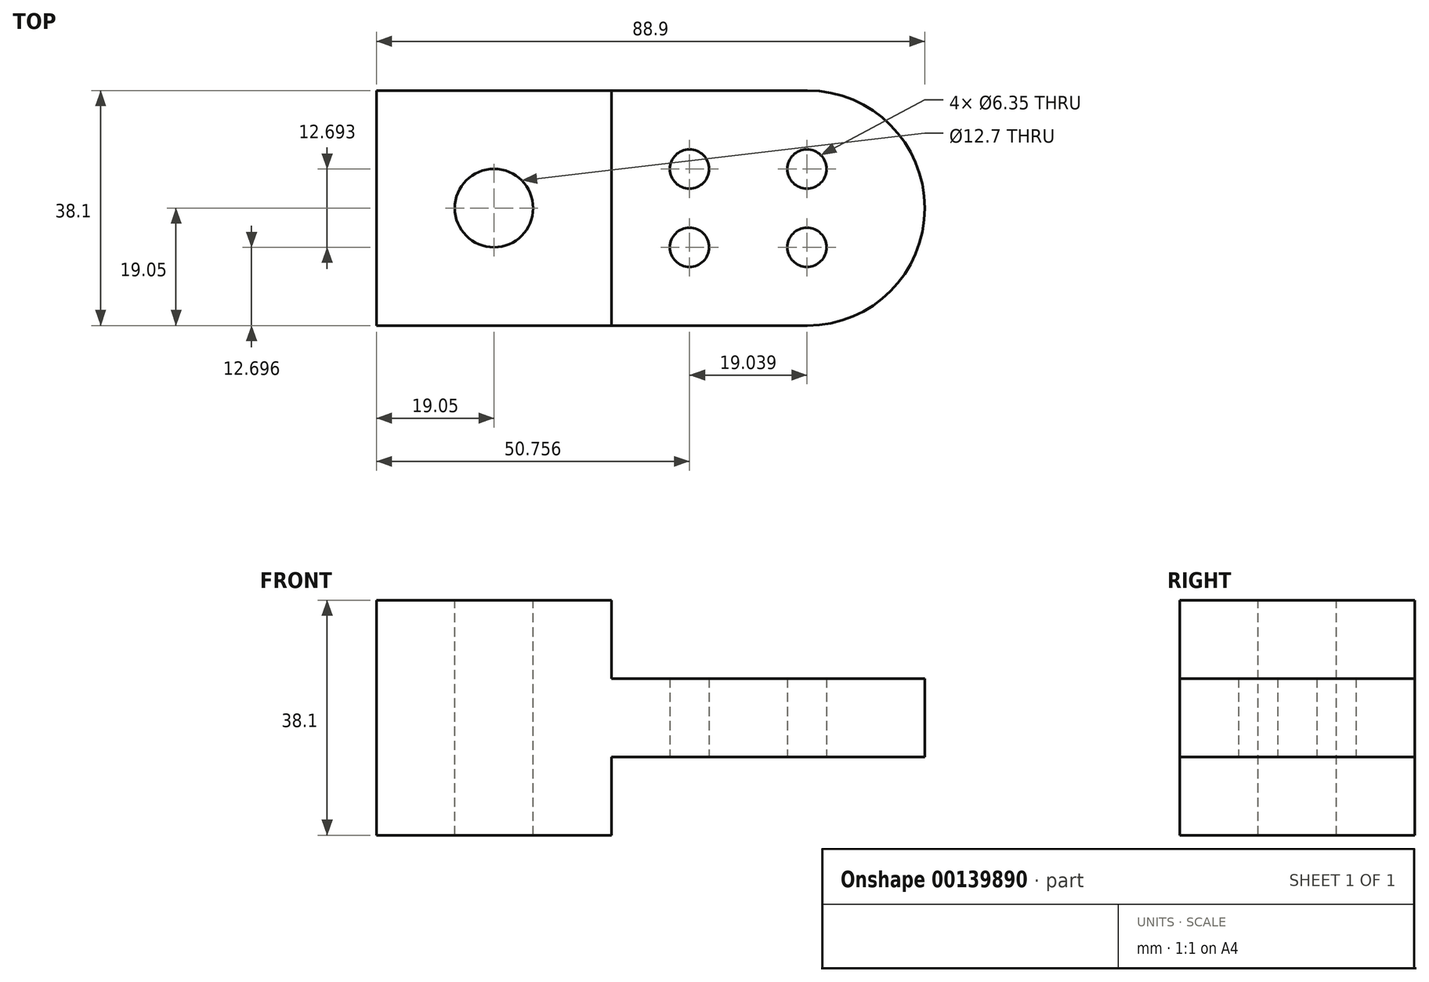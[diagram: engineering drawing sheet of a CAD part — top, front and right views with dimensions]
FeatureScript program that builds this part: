
annotation { "Feature Type Name" : "Feature", "Feature Type Description" : "" }
export const myFeature = defineFeature(function(context is Context, id is Id, definition is map)
    precondition{}
    {
        {
            var Q0;
            Q0=qCreatedBy(makeId("Top.planeOp"),FACE);
            var sketch = newSketch(context, id + "F0", { "sketchPlane" : qUnion([Q0])});
            skArc(sketch, "E0", {"start": v(88.9, -19.05) * mm, "mid": v(83.32, -5.58) * mm, "end": v(69.85, 0) * mm});
            skPoint(sketch, "E0.startSnap0", {"position": v(69.85, -19.05) * mm});
            skArc(sketch, "E1", {"start": v(69.85, -38.1) * mm, "mid": v(83.32, -32.52) * mm, "end": v(88.9, -19.05) * mm});
            skLineSegment(sketch, "E2", {"start": v(69.85, 0) * mm, "end": v(38.1, 0) * mm});
            skLineSegment(sketch, "E3", {"start": v(38.1, 0) * mm, "end": v(38.1, -38.1) * mm});
            skLineSegment(sketch, "E4", {"start": v(38.1, -38.1) * mm, "end": v(69.85, -38.1) * mm});
            skLineSegment(sketch, "E5", {"start": v(38.1, 0) * mm, "end": v(0, 0) * mm});
            skLineSegment(sketch, "E6", {"start": v(0, 0) * mm, "end": v(0, -38.1) * mm});
            skLineSegment(sketch, "E7", {"start": v(0, -38.1) * mm, "end": v(38.1, -38.1) * mm});
            skCircle(sketch, "E8", {"center": v(50.76, -12.71) * mm, "radius": 1.72 * mm});
            skCircle(sketch, "E9", {"center": v(50.76, -25.4) * mm, "radius": 1.91 * mm});
            skCircle(sketch, "E10", {"center": v(69.8, -25.4) * mm, "radius": 2.64 * mm});
            skCircle(sketch, "E11", {"center": v(69.8, -12.71) * mm, "radius": 2.7 * mm});
            skPoint(sketch, "E12.endSnap0", {"position": v(0, -19.05) * mm});
            skCircle(sketch, "E13", {"center": v(19.05, -19.05) * mm, "radius": 2.99 * mm});
            skPoint(sketch, "E13.centerSnap0", {"position": v(19.05, 0) * mm});
            skSolve(sketch);
        }
        {
            var Q0;
            Q0=makeQuery(id+"F0.imprint","IMPRINT",FACE,{"disambiguationData":[TD([[makeQuery(id+"F0.imprint","IMPRINT",EDGE,{"derivedFrom":sQuery(id+"F0.wireOp",EDGE,"E3")}),-1.0]])]});
            extrude(context, id + "F1", {"entities" : qUnion([Q0]), "depth" : 25.4 * mm, "hasSecondDirection" : true, "secondDirectionOppositeDirection" : true, "secondDirectionDepth" : 12.7 * mm});
        }
        {
            var Q0;
            Q0=makeQuery(id+"F0.imprint","IMPRINT",FACE,{"disambiguationData":[TD([[makeQuery(id+"F0.imprint","IMPRINT",EDGE,{"derivedFrom":sQuery(id+"F0.wireOp",EDGE,"E0")}),1.0]])]});
            extrude(context, id + "F2", {"entities" : qUnion([Q0]), "operationType" : NewBodyOperationType.ADD, "depth" : 12.7 * mm});
        }
        {
            var Q0;
            Q0=sQuery(id+"F0.wireOp",VERTEX,"E13.center");
            var Q1;
            Q1=makeQuery(id+"F1.opExtrude","SWEPT_BODY",BODY,{"disambiguationData":[OSD([sQuery(id+"F0.wireOp",EDGE,"E3"),sQuery(id+"F0.wireOp",EDGE,"E5"),sQuery(id+"F0.wireOp",EDGE,"E6"),sQuery(id+"F0.wireOp",EDGE,"E7"),sQuery(id+"F0.wireOp",EDGE,"UaYa9DtI-LoKc-IFyL-ACa9-g2jqe5lDBwFt")])]});
            hole(context, id + "F3", {"style" : HoleStyle.SIMPLE, "endStyle" : HoleEndStyle.THROUGH, "holeDiameter" : 12.7 * mm, "startFromSketch" : true, "locations" : qUnion([Q0]), "scope" : qUnion([Q1]), "isTappedThrough" : true});
        }
        {
            var Q0;
            Q0=sQuery(id+"F0.wireOp",VERTEX,"E13.center");
            var Q1;
            Q1=makeQuery(id+"F1.opExtrude","SWEPT_BODY",BODY,{"disambiguationData":[OSD([sQuery(id+"F0.wireOp",EDGE,"E3"),sQuery(id+"F0.wireOp",EDGE,"E5"),sQuery(id+"F0.wireOp",EDGE,"E6"),sQuery(id+"F0.wireOp",EDGE,"E7"),sQuery(id+"F0.wireOp",EDGE,"E13")])]});
            hole(context, id + "F4", {"style" : HoleStyle.SIMPLE, "endStyle" : HoleEndStyle.THROUGH, "oppositeDirection" : true, "holeDiameter" : 12.7 * mm, "startFromSketch" : true, "locations" : qUnion([Q0]), "scope" : qUnion([Q1]), "isTappedThrough" : true});
        }
        {
            var Q0;
            Q0=sQuery(id+"F0.wireOp",VERTEX,"E8.center");
            var Q1;
            Q1=sQuery(id+"F0.wireOp",VERTEX,"E11.center");
            var Q2;
            Q2=sQuery(id+"F0.wireOp",VERTEX,"E10.center");
            var Q3;
            Q3=sQuery(id+"F0.wireOp",VERTEX,"E9.center");
            var Q4;
            Q4=makeQuery(id+"F1.opExtrude","SWEPT_BODY",BODY,{"disambiguationData":[OSD([sQuery(id+"F0.wireOp",EDGE,"E3"),sQuery(id+"F0.wireOp",EDGE,"E5"),sQuery(id+"F0.wireOp",EDGE,"E6"),sQuery(id+"F0.wireOp",EDGE,"E7"),sQuery(id+"F0.wireOp",EDGE,"E13")])]});
            hole(context, id + "F5", {"style" : HoleStyle.SIMPLE, "endStyle" : HoleEndStyle.THROUGH, "oppositeDirection" : true, "holeDiameter" : 6.35 * mm, "startFromSketch" : true, "locations" : qUnion([Q0, Q1, Q2, Q3]), "scope" : qUnion([Q4]), "isTappedThrough" : true});
        }
    });
